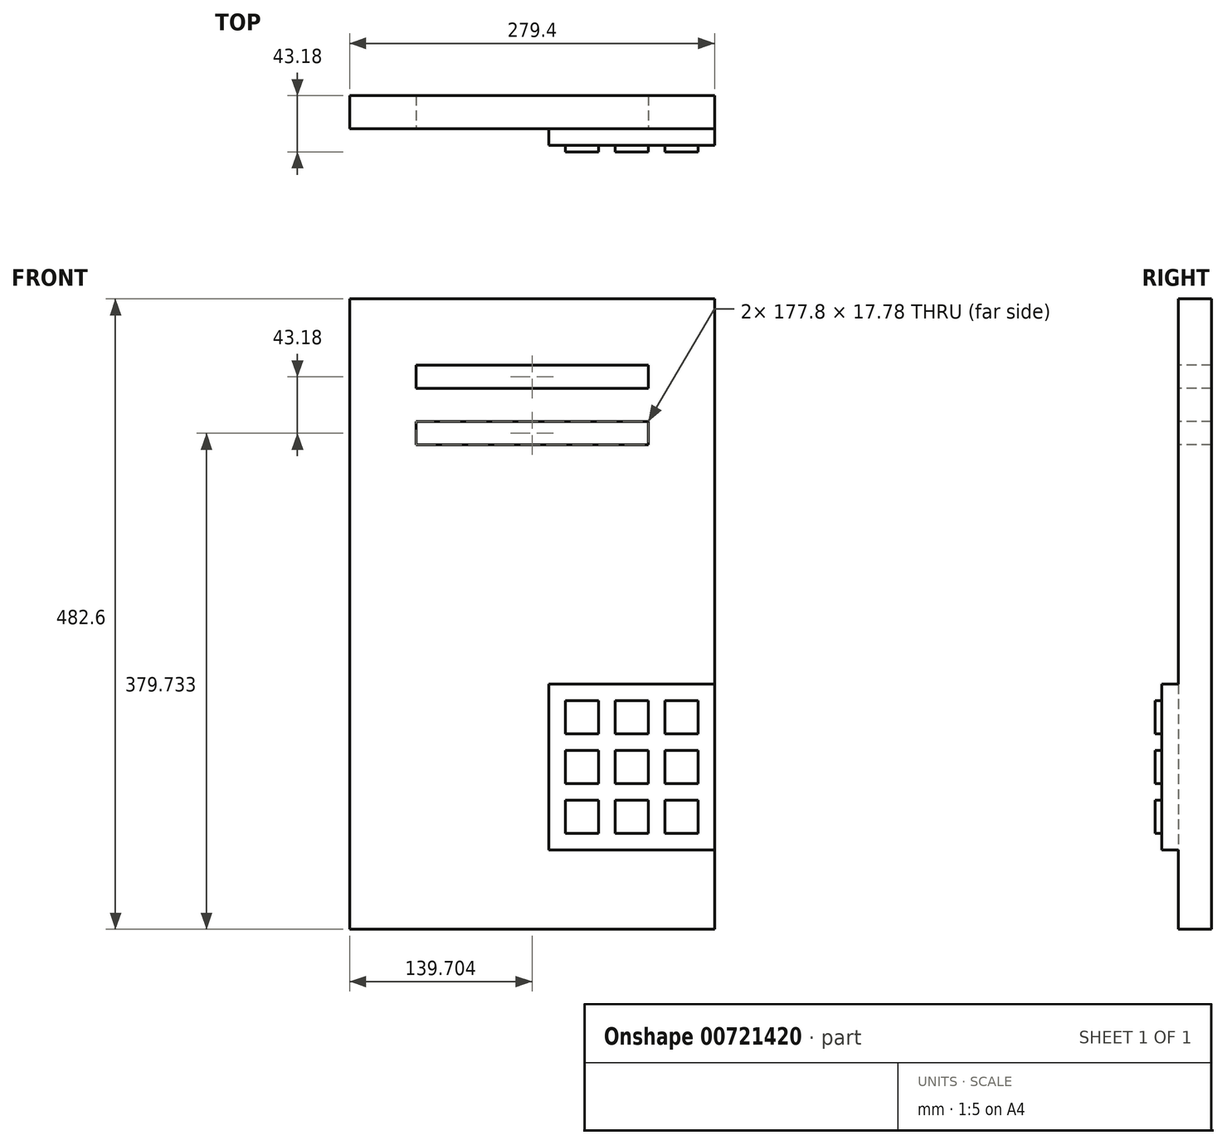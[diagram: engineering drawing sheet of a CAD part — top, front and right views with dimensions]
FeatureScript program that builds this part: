
annotation { "Feature Type Name" : "Feature", "Feature Type Description" : "" }
export const myFeature = defineFeature(function(context is Context, id is Id, definition is map)
    precondition{}
    {
        {
            var Q0;
            Q0=qCreatedBy(makeId("Front.planeOp"),FACE);
            var sketch = newSketch(context, id + "F0", { "sketchPlane" : qUnion([Q0])});
            skLineSegment(sketch, "E0.bottom", {"start": v(136.33, -187.72) * mm, "end": v(-143.07, -187.72) * mm});
            skLineSegment(sketch, "E0.top", {"start": v(136.33, 294.88) * mm, "end": v(-143.07, 294.88) * mm});
            skLineSegment(sketch, "E0.left", {"start": v(136.33, -187.72) * mm, "end": v(136.33, 294.88) * mm});
            skLineSegment(sketch, "E0.right", {"start": v(-143.07, -187.72) * mm, "end": v(-143.07, 294.88) * mm});
            skPoint(sketch, "E0.middle", {"position": v(-3.37, 53.58) * mm});
            skSolve(sketch);
        }
        {
            var Q0;
            Q0=makeQuery(id+"F0.imprint","IMPRINT",FACE,{"disambiguationData":[TD([[makeQuery(id+"F0.imprint","IMPRINT",EDGE,{"derivedFrom":sQuery(id+"F0.wireOp",EDGE,"E0.bottom")}),-1.0]])]});
            extrude(context, id + "F1", {"entities" : qUnion([Q0]), "depth" : 25.4 * mm, "offsetDistance" : 25.4 * mm});
        }
        {
            var Q0;
            Q0=makeQuery(id+"F1.opExtrude","CAP_FACE",FACE,{"disambiguationData":[OSD([sQuery(id+"F0.wireOp",EDGE,"E0.bottom"),sQuery(id+"F0.wireOp",EDGE,"E0.top"),sQuery(id+"F0.wireOp",EDGE,"E0.left"),sQuery(id+"F0.wireOp",EDGE,"E0.right")])],"isStart":false});
            var sketch = newSketch(context, id + "F2", { "sketchPlane" : qUnion([Q0])});
            skLineSegment(sketch, "E1.bottom", {"start": v(-92.27, 244.08) * mm, "end": v(85.53, 244.08) * mm});
            skLineSegment(sketch, "E1.top", {"start": v(-92.27, 226.3) * mm, "end": v(85.53, 226.3) * mm});
            skLineSegment(sketch, "E1.left", {"start": v(-92.27, 244.08) * mm, "end": v(-92.27, 226.3) * mm});
            skLineSegment(sketch, "E1.right", {"start": v(85.53, 244.08) * mm, "end": v(85.53, 226.3) * mm});
            skLineSegment(sketch, "E2.bottom", {"start": v(-92.27, 200.9) * mm, "end": v(85.53, 200.9) * mm});
            skLineSegment(sketch, "E2.top", {"start": v(-92.27, 183.12) * mm, "end": v(85.53, 183.12) * mm});
            skLineSegment(sketch, "E2.left", {"start": v(-92.27, 200.9) * mm, "end": v(-92.27, 183.12) * mm});
            skLineSegment(sketch, "E2.right", {"start": v(85.53, 200.9) * mm, "end": v(85.53, 183.12) * mm});
            skSolve(sketch);
        }
        {
            var Q0;
            Q0=makeQuery(id+"F2.imprint","IMPRINT",FACE,{"disambiguationData":[TD([[makeQuery(id+"F2.imprint","IMPRINT",EDGE,{"derivedFrom":sQuery(id+"F2.wireOp",EDGE,"E1.bottom")}),-1.0]])]});
            var Q1;
            Q1=makeQuery(id+"F2.imprint","IMPRINT",FACE,{"disambiguationData":[TD([[makeQuery(id+"F2.imprint","IMPRINT",EDGE,{"derivedFrom":sQuery(id+"F2.wireOp",EDGE,"E2.bottom")}),-1.0]])]});
            extrude(context, id + "F3", {"entities" : qUnion([Q0, Q1]), "operationType" : NewBodyOperationType.REMOVE, "oppositeDirection" : true, "depth" : 25.4 * mm, "offsetDistance" : 25.4 * mm});
        }
        {
            var Q0;
            Q0=makeQuery(id+"F1.opExtrude","CAP_FACE",FACE,{"disambiguationData":[OSD([sQuery(id+"F0.wireOp",EDGE,"E0.bottom"),sQuery(id+"F0.wireOp",EDGE,"E0.top"),sQuery(id+"F0.wireOp",EDGE,"E0.left"),sQuery(id+"F0.wireOp",EDGE,"E0.right")])],"isStart":false});
            var sketch = newSketch(context, id + "F4", { "sketchPlane" : qUnion([Q0])});
            skLineSegment(sketch, "E3.bottom", {"start": v(136.33, 0) * mm, "end": v(9.33, 0) * mm});
            skLineSegment(sketch, "E3.top", {"start": v(136.33, -127) * mm, "end": v(9.33, -127) * mm});
            skLineSegment(sketch, "E3.left", {"start": v(136.33, 0) * mm, "end": v(136.33, -127) * mm});
            skLineSegment(sketch, "E3.right", {"start": v(9.33, 0) * mm, "end": v(9.33, -127) * mm});
            skLineSegment(sketch, "E4.bottom", {"start": v(22.03, -12.7) * mm, "end": v(47.43, -12.7) * mm});
            skLineSegment(sketch, "E4.top", {"start": v(22.03, -38.1) * mm, "end": v(47.43, -38.1) * mm});
            skLineSegment(sketch, "E4.left", {"start": v(22.03, -12.7) * mm, "end": v(22.03, -38.1) * mm});
            skLineSegment(sketch, "E4.right", {"start": v(47.43, -12.7) * mm, "end": v(47.43, -38.1) * mm});
            skLineSegment(sketch, "E5.bottom", {"start": v(60.13, -12.7) * mm, "end": v(85.53, -12.7) * mm});
            skLineSegment(sketch, "E5.top", {"start": v(60.13, -38.1) * mm, "end": v(85.53, -38.1) * mm});
            skLineSegment(sketch, "E5.left", {"start": v(60.13, -12.7) * mm, "end": v(60.13, -38.1) * mm});
            skLineSegment(sketch, "E5.right", {"start": v(85.53, -12.7) * mm, "end": v(85.53, -38.1) * mm});
            skLineSegment(sketch, "E6.bottom", {"start": v(98.23, -12.7) * mm, "end": v(123.63, -12.7) * mm});
            skLineSegment(sketch, "E6.top", {"start": v(98.23, -38.1) * mm, "end": v(123.63, -38.1) * mm});
            skLineSegment(sketch, "E6.left", {"start": v(98.23, -12.7) * mm, "end": v(98.23, -38.1) * mm});
            skLineSegment(sketch, "E6.right", {"start": v(123.63, -12.7) * mm, "end": v(123.63, -38.1) * mm});
            skLineSegment(sketch, "E7.bottom", {"start": v(22.03, -50.8) * mm, "end": v(47.43, -50.8) * mm});
            skLineSegment(sketch, "E7.top", {"start": v(22.03, -76.2) * mm, "end": v(47.43, -76.2) * mm});
            skLineSegment(sketch, "E7.left", {"start": v(22.03, -50.8) * mm, "end": v(22.03, -76.2) * mm});
            skLineSegment(sketch, "E7.right", {"start": v(47.43, -50.8) * mm, "end": v(47.43, -76.2) * mm});
            skLineSegment(sketch, "E8.bottom", {"start": v(60.13, -50.8) * mm, "end": v(85.53, -50.8) * mm});
            skLineSegment(sketch, "E8.top", {"start": v(60.13, -76.2) * mm, "end": v(85.53, -76.2) * mm});
            skLineSegment(sketch, "E8.left", {"start": v(60.13, -50.8) * mm, "end": v(60.13, -76.2) * mm});
            skLineSegment(sketch, "E8.right", {"start": v(85.53, -50.8) * mm, "end": v(85.53, -76.2) * mm});
            skLineSegment(sketch, "E9.bottom", {"start": v(98.23, -50.8) * mm, "end": v(123.63, -50.8) * mm});
            skLineSegment(sketch, "E9.top", {"start": v(98.23, -76.2) * mm, "end": v(123.63, -76.2) * mm});
            skLineSegment(sketch, "E9.left", {"start": v(98.23, -50.8) * mm, "end": v(98.23, -76.2) * mm});
            skLineSegment(sketch, "E9.right", {"start": v(123.63, -50.8) * mm, "end": v(123.63, -76.2) * mm});
            skLineSegment(sketch, "E10.bottom", {"start": v(22.03, -88.9) * mm, "end": v(47.43, -88.9) * mm});
            skLineSegment(sketch, "E10.top", {"start": v(22.03, -114.3) * mm, "end": v(47.43, -114.3) * mm});
            skLineSegment(sketch, "E10.left", {"start": v(22.03, -88.9) * mm, "end": v(22.03, -114.3) * mm});
            skLineSegment(sketch, "E10.right", {"start": v(47.43, -88.9) * mm, "end": v(47.43, -114.3) * mm});
            skLineSegment(sketch, "E11.bottom", {"start": v(60.13, -114.3) * mm, "end": v(85.53, -114.3) * mm});
            skLineSegment(sketch, "E11.top", {"start": v(60.13, -88.9) * mm, "end": v(85.53, -88.9) * mm});
            skLineSegment(sketch, "E11.left", {"start": v(60.13, -114.3) * mm, "end": v(60.13, -88.9) * mm});
            skLineSegment(sketch, "E11.right", {"start": v(85.53, -114.3) * mm, "end": v(85.53, -88.9) * mm});
            skLineSegment(sketch, "E12.bottom", {"start": v(123.63, -114.3) * mm, "end": v(98.23, -114.3) * mm});
            skLineSegment(sketch, "E12.top", {"start": v(123.63, -88.9) * mm, "end": v(98.23, -88.9) * mm});
            skLineSegment(sketch, "E12.left", {"start": v(123.63, -114.3) * mm, "end": v(123.63, -88.9) * mm});
            skLineSegment(sketch, "E12.right", {"start": v(98.23, -114.3) * mm, "end": v(98.23, -88.9) * mm});
            skSolve(sketch);
        }
        {
            var Q0;
            Q0=makeQuery(id+"F4.imprint","IMPRINT",FACE,{"disambiguationData":[TD([[makeQuery(id+"F4.imprint","IMPRINT",EDGE,{"derivedFrom":sQuery(id+"F4.wireOp",EDGE,"E10.bottom")}),-1.0]])]});
            var Q1;
            Q1=makeQuery(id+"F4.imprint","IMPRINT",FACE,{"disambiguationData":[TD([[makeQuery(id+"F4.imprint","IMPRINT",EDGE,{"derivedFrom":sQuery(id+"F4.wireOp",EDGE,"E11.bottom")}),1.0]])]});
            var Q2;
            Q2=makeQuery(id+"F4.imprint","IMPRINT",FACE,{"disambiguationData":[TD([[makeQuery(id+"F4.imprint","IMPRINT",EDGE,{"derivedFrom":sQuery(id+"F4.wireOp",EDGE,"E12.bottom")}),-1.0]])]});
            var Q3;
            Q3=makeQuery(id+"F4.imprint","IMPRINT",FACE,{"disambiguationData":[TD([[makeQuery(id+"F4.imprint","IMPRINT",EDGE,{"derivedFrom":sQuery(id+"F4.wireOp",EDGE,"E9.bottom")}),-1.0]])]});
            var Q4;
            Q4=makeQuery(id+"F4.imprint","IMPRINT",FACE,{"disambiguationData":[TD([[makeQuery(id+"F4.imprint","IMPRINT",EDGE,{"derivedFrom":sQuery(id+"F4.wireOp",EDGE,"E8.bottom")}),-1.0]])]});
            var Q5;
            Q5=makeQuery(id+"F4.imprint","IMPRINT",FACE,{"disambiguationData":[TD([[makeQuery(id+"F4.imprint","IMPRINT",EDGE,{"derivedFrom":sQuery(id+"F4.wireOp",EDGE,"E7.bottom")}),-1.0]])]});
            var Q6;
            Q6=makeQuery(id+"F4.imprint","IMPRINT",FACE,{"disambiguationData":[TD([[makeQuery(id+"F4.imprint","IMPRINT",EDGE,{"derivedFrom":sQuery(id+"F4.wireOp",EDGE,"E4.bottom")}),-1.0]])]});
            var Q7;
            Q7=makeQuery(id+"F4.imprint","IMPRINT",FACE,{"disambiguationData":[TD([[makeQuery(id+"F4.imprint","IMPRINT",EDGE,{"derivedFrom":sQuery(id+"F4.wireOp",EDGE,"E5.bottom")}),-1.0]])]});
            var Q8;
            Q8=makeQuery(id+"F4.imprint","IMPRINT",FACE,{"disambiguationData":[TD([[makeQuery(id+"F4.imprint","IMPRINT",EDGE,{"derivedFrom":sQuery(id+"F4.wireOp",EDGE,"E6.bottom")}),-1.0]])]});
            extrude(context, id + "F5", {"entities" : qUnion([Q0, Q1, Q2, Q3, Q4, Q5, Q6, Q7, Q8]), "operationType" : NewBodyOperationType.ADD, "depth" : 17.78 * mm, "offsetDistance" : 25.4 * mm});
        }
        {
            var Q0;
            Q0=makeQuery(id+"F4.imprint","IMPRINT",FACE,{"disambiguationData":[TD([[makeQuery(id+"F4.imprint","IMPRINT",EDGE,{"derivedFrom":sQuery(id+"F4.wireOp",EDGE,"E3.bottom")}),1.0]])]});
            extrude(context, id + "F6", {"entities" : qUnion([Q0]), "operationType" : NewBodyOperationType.ADD, "depth" : 12.7 * mm, "offsetDistance" : 25.4 * mm});
        }
    });
